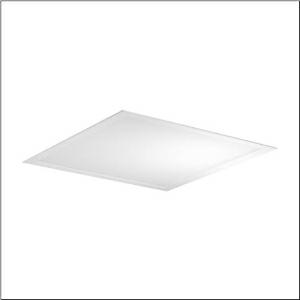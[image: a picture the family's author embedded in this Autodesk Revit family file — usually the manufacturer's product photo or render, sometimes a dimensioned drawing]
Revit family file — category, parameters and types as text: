
# Revit family: apollon_21_square_51mq11wd2t14
name_source: partatom
category: Lighting Fixtures
units: mm (PartAtom-declared; Revit-internal decimal feet)

## family parameters
Cut with Voids When Loaded = No
Host = Face
Light Source = No
Part Type = Normal
Room Calculation Point = No
Round Connector Dimension = Use Diameter
Shared = No

## types (1)
- --- (1 x LED 2700 K ... 6500 K, 4600 lm, 30.4 W, 4000K)
    Apparent Load = 30 VA
    CIE Flux Codes = 66 89 97 100 100
    Color Rendering = 80
    Color Temperature = 4000K
    Default Elevation = 1800 mm
    Description = Apollon 21 square, office luminaire, primary optical cover: micro prismatic cover, of PMMA, CAT 2 (L<= 3000cd/m²), light emission: direct distribution, primary light characteristic: symmetric, installation type: lay-in mounting, LED, rated luminous flux: 4.600lm, luminous efficacy: 151lm/W, light colour: 8tw, colour temperature: 2700..6500K, control gear: DALI-2 DT8, with terminal, 5-pole, mains connection: 220..240V, AC/DC, 0/50..60Hz, rated input power: 30.4W, suitable for self-contained emergency lighting element 59MQE002602A with integrated self-test function according to EN 60598-2-22, housing, of aluminium, coated, traffic white (RAL 9016), module: M625, length: 620mm, width: 620mm, height: 55mm, recess depth: 180mm, housing upper side, of sheet steel, galvanised, protection rating (complete): IP20, protection rating (lamp compartment, on room side): IP50, insulation class (complete): insulation class II (safety insulation), certification: CE, ENEC, impact resistance: IK03, permissible operating ambient temperature: -20..+45°C, permissible storage temperature: -40..+80°C, standard: EN 60598-2-22, packaging unit: 1 piece
    Height = 0 mm  [stored 0 ft]
    Lamp = 1 x LED 2700 K ... 6500 K
    Lamp Light Flux = 4600 lm
    Lamp Power = 30.4 W
    Lamp count = 1
    Length = 620 mm
    Luminous efficacy = 151 lm/W
    Manufacturer = Siteco
    ModVariant = No
    Model = 51MQ11WD2T14
    Mounting Place = Ceiling
    Mounting Type = Recessed
    Number of Poles = 1
    OnlyDefault = Yes
    Power Factor = 1
    Product Name = Apollon 21 square
    Product group = office luminaire | ceiling recessed
    ProductGroupID = 400
    Protection Class = Protection class II
    Protection Degree = IP 20
    RLX_Detail_Level = 1
    RLX_Emergency_Light_Flux = 0 lm
    RLX_Emergency_Type = 0
    RLX_Emergency_Type_DB = No
    RlxData = <blob elided: 13205 chars, md5=b8335ce8>
    Socket = socket
    Standby Power = 0 W
    System Light Flux = 4600 lm
    System Power = 30 W
    Type Comments = factory setting: CCT=4000K, colour temperature 4000K
    Type Image = l_1291054.jpg
    URL = http://relux.com
    VarID = @adj_088685
    Voltage = 0 V
    Weight = 0.00 kg
    Width = 620 mm

note: [stored X ft] marks values corroborated as IEEE doubles in the binary element streams (Revit-internal decimal feet)

## geometry (parser evidence)
native form markers: Sweep x11
no freeform markers — native parametric forms only
